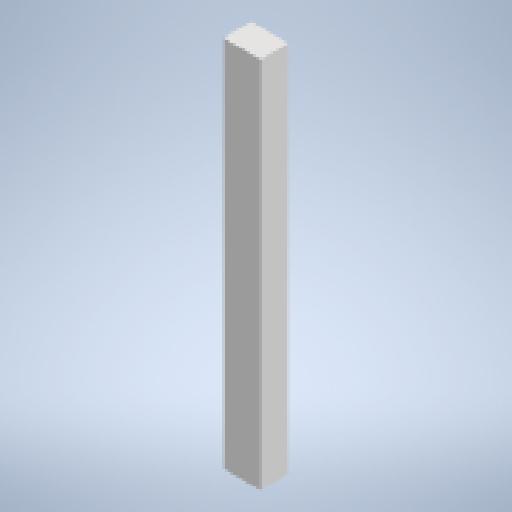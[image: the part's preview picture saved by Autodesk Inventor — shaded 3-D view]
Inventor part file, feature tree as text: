
AUTODESK INVENTOR PART (.ipt)
format: ipt  version: 2024 (Build 280153000, 153)  size: 139,776 bytes
history: native  units: mm
features: extrude x1, sketch x1
ambient origin geometry x8: Origin, YZ Plane, XZ Plane, XY Plane, X Axis, Y Axis, Z Axis, Center Point
bodies: Solido1 (feature_tree)
feature tree (2):
  extrude  "Estrusione1"  Depth=400.0mm
  sketch  "Schizzo1"
